# Revit family: Haworth_Enclose_Door_DoubleSwing
name_source: partatom
category: Furniture Systems
revit_build: Autodesk Revit 2018 (Build: 20170223_1515(x64)
units: mm (PartAtom-declared; Revit-internal decimal feet)

## family parameters
Always vertical = Yes
Cut with Voids When Loaded = No
OmniClass Number = 23.25.40.14
OmniClass Title = Demountable Partitions
Part Type = Normal
Room Calculation Point = No
Round Connector Dimension = Use Diameter
Shared = Yes
Work Plane-Based = No

## types (4) — shared parameters
# of Muntins = 2
AFF Muntin 1 = 28 "
AFF Muntin 2 = 54 "
Actual # of Muntins = 2
Actual AFF Muntin 1 = 28 "
Actual AFF Muntin 2 = 54 "
Actual Door Height = 104.5 "
Actual Height = 108 "
Assembly Code = C1010200
Base Height = 1.25 "
Bottom Rail Width = 5.235 "
Cap Height = 1 "
Ceiling Mount = Yes
Circular Plate = No
Description = Double Swing
Door Finish = Haworth _ Paint _ Smoke
Door Hardware Finish = Haworth _ Metal _ Brushed Aluminum
Door Height = 104.5 "
Door Pull Length = 16 "
Door Pull Offset = 1.66 "
End of Run Finish = Haworth _ Polymer _ Black
End of Run Width = 0.155 "
Frame Depth = 4 "
Frame Finish = Haworth _ Metal _ Brushed Aluminum
Glass Finish = Haworth _ Glass _ Clear
Glass Offset = 5.235 "
Glass Slab Door = No
Glazed Door = Yes
Height = 108 "
Horizontal Frame Width = 0.875 "
Horizontal Top Adjuster Width = 2.625 "
Horizontal Top Trim Width = 1.5 "
Lever = No
Lever Plate = No
Manufacturer = Haworth
Material Options = http://surfaces.haworth.com
Max # of Muntins = 2
Max. Height = 120 "
Max. Width = 96 "
Metal Glazed Door = Yes
Min. Height = 84 "
Min. Spacing Between Muntins = 8 "
Min. Width = 48 "
Min/Max Height = 84-120 in.
Min/Max Width = 24-48 in.
Model = Haworth - Enclose Door
Muntin Finish = Haworth _ Metal _ Brushed Aluminum
Muntin Note = Bottom Muntin is Muntin 1
Muntin Width = 0.875 "
Non Locking_Glass Slab Only = No
Panel Depth = 0.5 "
Panel Height = 8 "
Pull Height Centerline = 40 "
Rectilinear D Pull = No
Revision Number = 3
Size = Verify Final Dim. w/ Haworth
Style Width = 5.355 "
Sustainability Info = http://www.haworth.com
Too Many Muntins = No
Top Rail Width = 5.235 "
Tubular D Pull = Yes
URL = www.haworth.com
URL - Product = http://www.haworth.com
Vertical Frame Width = 0.875 "
Warranty = http://www.haworth.com
Wood Door = No
Wood Glazed Door = No

## per-type parameters (varying)
| type | Actual Door Width | Actual Width | Door Leaf Width | Mortise Lock_Glass Slab Only | Overall Door Opening | Panel Width | Pull Offset Centerline | Width |
| 72" x 108" | 34.97 " | 72 " | 34.97 " | No | 69.94 " | 69.94 " | 2.755 " | 72 " |
| 48" x 108" | 22.97 " | 48 " | 22.97 " | Yes | 45.94 " | 45.94 " | 2.47 " | 48 " |
| 60" x 108" | 28.97 " | 60 " | 28.97 " | Yes | 57.94 " | 57.94 " | 2.47 " | 60 " |
| 96" x 108" | 46.97 " | 96 " | 46.97 " | Yes | 93.94 " | 93.94 " | 2.47 " | 96 " |

## geometry (parser evidence)
native form markers: Blend x2, Sweep x16
no freeform markers — native parametric forms only
